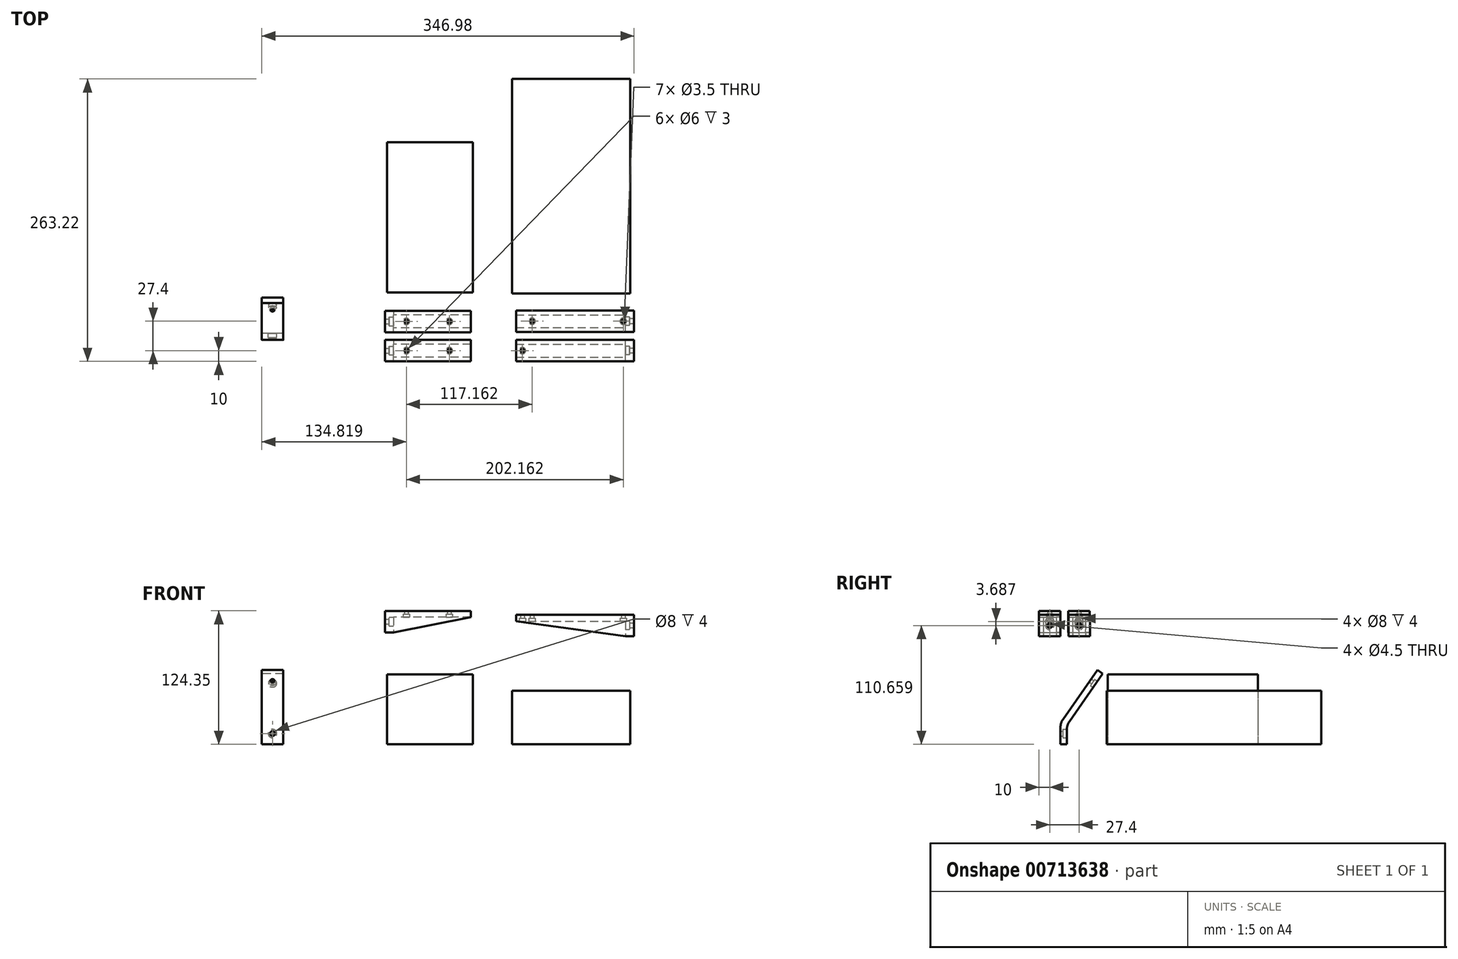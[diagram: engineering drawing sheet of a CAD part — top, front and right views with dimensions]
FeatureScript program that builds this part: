
annotation { "Feature Type Name" : "Feature", "Feature Type Description" : "" }
export const myFeature = defineFeature(function(context is Context, id is Id, definition is map)
    precondition{}
    {
        {
            var Q0;
            Q0=qCreatedBy(makeId("Right.planeOp"),FACE);
            var sketch = newSketch(context, id + "F0", { "sketchPlane" : qUnion([Q0])});
            skLineSegment(sketch, "E0", {"start": v(0, 0) * mm, "end": v(6, 0) * mm});
            skLineSegment(sketch, "E1", {"start": v(6, 0) * mm, "end": v(6, 18.1) * mm});
            skLineSegment(sketch, "E2", {"start": v(6, 18.1) * mm, "end": v(39.33, 65.7) * mm});
            skLineSegment(sketch, "E3", {"start": v(39.33, 65.7) * mm, "end": v(34.41, 69.15) * mm});
            skLineSegment(sketch, "E4", {"start": v(34.41, 69.15) * mm, "end": v(0, 20) * mm});
            skLineSegment(sketch, "E5", {"start": v(0, 20) * mm, "end": v(0, 0) * mm});
            skSolve(sketch);
        }
        {
            var Q0;
            Q0=makeQuery(id+"F0.imprint","IMPRINT",FACE,{"disambiguationData":[TD([[makeQuery(id+"F0.imprint","IMPRINT",EDGE,{"derivedFrom":sQuery(id+"F0.wireOp",EDGE,"E0")}),1.0]])]});
            extrude(context, id + "F1", {"entities" : qUnion([Q0]), "depth" : 20 * mm});
        }
        {
            var Q0;
            Q0=makeQuery(id+"F1.opExtrude","SWEPT_FACE",FACE,{"disambiguationData":[OSD([sQuery(id+"F0.wireOp",EDGE,"E1")])]});
            var sketch = newSketch(context, id + "F2", { "sketchPlane" : qUnion([Q0])});
            skCircle(sketch, "E6", {"center": v(-10, 10) * mm, "radius": 2.25 * mm});
            skPoint(sketch, "E6.centerSnap0", {"position": v(-10, 0) * mm});
            skCircle(sketch, "E7", {"center": v(-10, 10) * mm, "radius": 4 * mm});
            skSolve(sketch);
        }
        {
            var Q0;
            Q0=makeQuery(id+"F1.opExtrude","SWEPT_FACE",FACE,{"disambiguationData":[OSD([sQuery(id+"F0.wireOp",EDGE,"E4")])]});
            var sketch = newSketch(context, id + "F3", { "sketchPlane" : qUnion([Q0])});
            skCircle(sketch, "E8", {"center": v(10, 64.38) * mm, "radius": 1.75 * mm});
            skPoint(sketch, "E8.centerSnap0", {"position": v(10, 16.38) * mm});
            skCircle(sketch, "E9", {"center": v(10, 64.38) * mm, "radius": 3.5 * mm});
            skSolve(sketch);
        }
        {
            var Q0;
            Q0=makeQuery(id+"F3.imprint","IMPRINT",FACE,{"disambiguationData":[TD([[makeQuery(id+"F3.imprint","IMPRINT",EDGE,{"derivedFrom":sQuery(id+"F3.wireOp",EDGE,"E8")}),1.0]])]});
            extrude(context, id + "F4", {"entities" : qUnion([Q0]), "operationType" : NewBodyOperationType.REMOVE, "oppositeDirection" : true, "depth" : 25 * mm});
        }
        {
            var Q0;
            Q0=makeQuery(id+"F1.opExtrude","SWEPT_FACE",FACE,{"disambiguationData":[OSD([sQuery(id+"F0.wireOp",EDGE,"E2")])]});
            var sketch = newSketch(context, id + "F5", { "sketchPlane" : qUnion([Q0])});
            skCircle(sketch, "E10", {"center": v(-10, 64.38) * mm, "radius": 3.5 * mm});
            skSolve(sketch);
        }
        {
            var Q0;
            Q0=makeQuery(id+"F5.imprint","IMPRINT",FACE,{"disambiguationData":[TD([[makeQuery(id+"F5.imprint","IMPRINT",EDGE,{"derivedFrom":sQuery(id+"F5.wireOp",EDGE,"E10")}),1.0]])]});
            extrude(context, id + "F6", {"entities" : qUnion([Q0]), "operationType" : NewBodyOperationType.REMOVE, "oppositeDirection" : true, "depth" : 3 * mm});
        }
        {
            var Q0;
            Q0=makeQuery(id+"F2.imprint","IMPRINT",FACE,{"disambiguationData":[TD([[makeQuery(id+"F2.imprint","IMPRINT",EDGE,{"derivedFrom":sQuery(id+"F2.wireOp",EDGE,"E6")}),1.0]])]});
            extrude(context, id + "F7", {"entities" : qUnion([Q0]), "operationType" : NewBodyOperationType.REMOVE, "oppositeDirection" : true, "depth" : 25 * mm});
        }
        {
            var Q0;
            Q0=makeQuery(id+"F2.imprint","IMPRINT",FACE,{"disambiguationData":[TD([[makeQuery(id+"F2.imprint","IMPRINT",EDGE,{"derivedFrom":sQuery(id+"F2.wireOp",EDGE,"E6")}),-1.0]])]});
            extrude(context, id + "F8", {"entities" : qUnion([Q0]), "operationType" : NewBodyOperationType.REMOVE, "oppositeDirection" : true, "depth" : 4 * mm});
        }
        {
            var Q0;
            Q0=makeQuery(id+"F1.opExtrude","SWEPT_EDGE",EDGE,{"disambiguationData":[OSD([sQuery(id+"F0.wireOp",EDGE,"E1"),sQuery(id+"F0.wireOp",EDGE,"E2")])]});
            var Q1;
            Q1=makeQuery(id+"F1.opExtrude","SWEPT_EDGE",EDGE,{"disambiguationData":[OSD([sQuery(id+"F0.wireOp",EDGE,"E4"),sQuery(id+"F0.wireOp",EDGE,"E5")])]});
            fillet(context, id + "F9", {"entities" : qUnion([Q0, Q1]), "radius" : 13 * mm, "tangentPropagation" : true, "allowEdgeOverflow" : false});
        }
        {
            var Q0;
            Q0=qCreatedBy(makeId("Top.planeOp"),FACE);
            var sketch = newSketch(context, id + "F10", { "sketchPlane" : qUnion([Q0])});
            skLineSegment(sketch, "E11.bottom", {"start": v(116.68, 184.13) * mm, "end": v(196.68, 184.13) * mm});
            skLineSegment(sketch, "E11.top", {"start": v(116.68, 44.13) * mm, "end": v(196.68, 44.13) * mm});
            skLineSegment(sketch, "E11.left", {"start": v(116.68, 184.13) * mm, "end": v(116.68, 44.13) * mm});
            skLineSegment(sketch, "E11.right", {"start": v(196.68, 184.13) * mm, "end": v(196.68, 44.13) * mm});
            skSolve(sketch);
        }
        {
            var Q0;
            Q0=makeQuery(id+"F10.imprint","IMPRINT",FACE,{"disambiguationData":[TD([[makeQuery(id+"F10.imprint","IMPRINT",EDGE,{"derivedFrom":sQuery(id+"F10.wireOp",EDGE,"E11.bottom")}),-1.0]])]});
            extrude(context, id + "F11", {"entities" : qUnion([Q0]), "depth" : 65 * mm});
        }
        {
            var Q0;
            Q0=qCreatedBy(makeId("Top.planeOp"),FACE);
            var sketch = newSketch(context, id + "F12", { "sketchPlane" : qUnion([Q0])});
            skLineSegment(sketch, "E12.bottom", {"start": v(233.36, 43.22) * mm, "end": v(343.36, 43.22) * mm});
            skLineSegment(sketch, "E12.top", {"start": v(233.36, 243.22) * mm, "end": v(343.36, 243.22) * mm});
            skLineSegment(sketch, "E12.left", {"start": v(233.36, 43.22) * mm, "end": v(233.36, 243.22) * mm});
            skLineSegment(sketch, "E12.right", {"start": v(343.36, 43.22) * mm, "end": v(343.36, 243.22) * mm});
            skSolve(sketch);
        }
        {
            var Q0;
            Q0=makeQuery(id+"F12.imprint","IMPRINT",FACE,{"disambiguationData":[TD([[makeQuery(id+"F12.imprint","IMPRINT",EDGE,{"derivedFrom":sQuery(id+"F12.wireOp",EDGE,"E12.bottom")}),1.0]])]});
            extrude(context, id + "F13", {"entities" : qUnion([Q0]), "depth" : 50 * mm});
        }
        {
            var Q0;
            Q0=qCreatedBy(makeId("Front.planeOp"),FACE);
            var sketch = newSketch(context, id + "F14", { "sketchPlane" : qUnion([Q0])});
            skLineSegment(sketch, "E13", {"start": v(114.82, 104.35) * mm, "end": v(122.82, 104.35) * mm});
            skLineSegment(sketch, "E14", {"start": v(114.82, 104.35) * mm, "end": v(114.82, 124.35) * mm});
            skLineSegment(sketch, "E15", {"start": v(114.82, 124.35) * mm, "end": v(194.82, 124.35) * mm});
            skLineSegment(sketch, "E16", {"start": v(194.82, 124.35) * mm, "end": v(194.82, 118.35) * mm});
            skLineSegment(sketch, "E17", {"start": v(194.82, 118.35) * mm, "end": v(122.82, 118.35) * mm});
            skLineSegment(sketch, "E18", {"start": v(122.82, 118.35) * mm, "end": v(122.82, 104.35) * mm});
            skSolve(sketch);
        }
        {
            var Q0;
            Q0=makeQuery(id+"F14.imprint","IMPRINT",FACE,{"disambiguationData":[TD([[makeQuery(id+"F14.imprint","IMPRINT",EDGE,{"derivedFrom":sQuery(id+"F14.wireOp",EDGE,"E13")}),1.0]])]});
            extrude(context, id + "F15", {"entities" : qUnion([Q0]), "depth" : 20 * mm});
        }
        {
            var Q0;
            Q0=makeQuery(id+"F15.opExtrude","SWEPT_FACE",FACE,{"disambiguationData":[OSD([sQuery(id+"F14.wireOp",EDGE,"E18")])]});
            var sketch = newSketch(context, id + "F16", { "sketchPlane" : qUnion([Q0])});
            skCircle(sketch, "E19", {"center": v(-10, 114.35) * mm, "radius": 2.25 * mm});
            skPoint(sketch, "E19.centerSnap0", {"position": v(-10, 104.35) * mm});
            skCircle(sketch, "E20", {"center": v(-10, 114.35) * mm, "radius": 4 * mm});
            skSolve(sketch);
        }
        {
            var Q0;
            Q0=makeQuery(id+"F16.imprint","IMPRINT",FACE,{"disambiguationData":[TD([[makeQuery(id+"F16.imprint","IMPRINT",EDGE,{"derivedFrom":sQuery(id+"F16.wireOp",EDGE,"E19")}),1.0]])]});
            extrude(context, id + "F17", {"entities" : qUnion([Q0]), "operationType" : NewBodyOperationType.REMOVE, "endBound" : BoundingType.THROUGH_ALL, "oppositeDirection" : true, "depth" : 25 * mm});
        }
        {
            var Q0;
            Q0=makeQuery(id+"F16.imprint","IMPRINT",FACE,{"disambiguationData":[TD([[makeQuery(id+"F16.imprint","IMPRINT",EDGE,{"derivedFrom":sQuery(id+"F16.wireOp",EDGE,"E19")}),-1.0]])]});
            extrude(context, id + "F18", {"entities" : qUnion([Q0]), "operationType" : NewBodyOperationType.REMOVE, "oppositeDirection" : true, "depth" : 4 * mm});
        }
        {
            var Q0;
            Q0=makeQuery(id+"F15.opExtrude","CAP_VERTEX",VERTEX,{"disambiguationData":[OSD([sQuery(id+"F14.wireOp",EDGE,"E13"),sQuery(id+"F14.wireOp",EDGE,"E18")])],"isStart":false});
            var Q1;
            Q1=makeQuery(id+"F15.opExtrude","CAP_VERTEX",VERTEX,{"disambiguationData":[OSD([sQuery(id+"F14.wireOp",EDGE,"E13"),sQuery(id+"F14.wireOp",EDGE,"E18")])],"isStart":true});
            var Q2;
            Q2=makeQuery(id+"F15.opExtrude","CAP_VERTEX",VERTEX,{"disambiguationData":[OSD([sQuery(id+"F14.wireOp",EDGE,"E16"),sQuery(id+"F14.wireOp",EDGE,"E17")])],"isStart":false});
            cPlane(context, id + "F19", {"entities" : qUnion([Q0, Q1, Q2]), "cplaneType" : CPlaneType.THREE_POINT, "offset" : 25 * mm, "width" : 150 * mm, "height" : 150 * mm});
        }
        {
            var Q0;
            Q0=qCreatedBy(id+"F19.planeOp",FACE);
            var sketch = newSketch(context, id + "F20", { "sketchPlane" : qUnion([Q0])});
            skLineSegment(sketch, "E21.bottom", {"start": v(140.48, -20) * mm, "end": v(213.83, -20) * mm});
            skLineSegment(sketch, "E21.top", {"start": v(140.48, -16) * mm, "end": v(213.83, -16) * mm});
            skLineSegment(sketch, "E21.left", {"start": v(140.48, -20) * mm, "end": v(140.48, -16) * mm});
            skLineSegment(sketch, "E21.right", {"start": v(213.83, -20) * mm, "end": v(213.83, -16) * mm});
            skLineSegment(sketch, "E22.bottom", {"start": v(140.48, 0) * mm, "end": v(213.83, 0) * mm});
            skLineSegment(sketch, "E22.top", {"start": v(140.48, -4) * mm, "end": v(213.83, -4) * mm});
            skLineSegment(sketch, "E22.left", {"start": v(140.48, 0) * mm, "end": v(140.48, -4) * mm});
            skLineSegment(sketch, "E22.right", {"start": v(213.83, 0) * mm, "end": v(213.83, -4) * mm});
            skSolve(sketch);
        }
        {
            var Q0;
            Q0=qSketchRegion(id+"F20",true);
            extrude(context, id + "F21", {"entities" : qUnion([Q0]), "operationType" : NewBodyOperationType.ADD, "endBound" : BoundingType.UP_TO_NEXT, "depth" : 25 * mm});
        }
        {
            var Q0;
            Q0=makeQuery(id+"F15.opExtrude","SWEPT_FACE",FACE,{"disambiguationData":[OSD([sQuery(id+"F14.wireOp",EDGE,"E17")])]});
            var sketch = newSketch(context, id + "F22", { "sketchPlane" : qUnion([Q0])});
            skCircle(sketch, "E23", {"center": v(174.82, 10) * mm, "radius": 1.75 * mm});
            skPoint(sketch, "E23.centerSnap0", {"position": v(194.82, 10) * mm});
            skCircle(sketch, "E24", {"center": v(174.82, 10) * mm, "radius": 3 * mm});
            skCircle(sketch, "E25", {"center": v(134.82, 10) * mm, "radius": 1.75 * mm});
            skCircle(sketch, "E26", {"center": v(134.82, 10) * mm, "radius": 3 * mm});
            skSolve(sketch);
        }
        {
            var Q0;
            Q0=makeQuery(id+"F22.imprint","IMPRINT",FACE,{"disambiguationData":[TD([[makeQuery(id+"F22.imprint","IMPRINT",EDGE,{"derivedFrom":sQuery(id+"F22.wireOp",EDGE,"E25")}),1.0]])]});
            var Q1;
            Q1=makeQuery(id+"F22.imprint","IMPRINT",FACE,{"disambiguationData":[TD([[makeQuery(id+"F22.imprint","IMPRINT",EDGE,{"derivedFrom":sQuery(id+"F22.wireOp",EDGE,"E23")}),1.0]])]});
            extrude(context, id + "F23", {"entities" : qUnion([Q0, Q1]), "operationType" : NewBodyOperationType.REMOVE, "endBound" : BoundingType.THROUGH_ALL, "oppositeDirection" : true, "depth" : 25 * mm});
        }
        {
            var Q0;
            Q0=makeQuery(id+"F22.imprint","IMPRINT",FACE,{"disambiguationData":[TD([[makeQuery(id+"F22.imprint","IMPRINT",EDGE,{"derivedFrom":sQuery(id+"F22.wireOp",EDGE,"E25")}),-1.0]])]});
            var Q1;
            Q1=makeQuery(id+"F22.imprint","IMPRINT",FACE,{"disambiguationData":[TD([[makeQuery(id+"F22.imprint","IMPRINT",EDGE,{"derivedFrom":sQuery(id+"F22.wireOp",EDGE,"E23")}),-1.0]])]});
            extrude(context, id + "F24", {"entities" : qUnion([Q0, Q1]), "operationType" : NewBodyOperationType.REMOVE, "oppositeDirection" : true, "depth" : 3 * mm});
        }
        {
            var Q0;
            Q0=qCreatedBy(makeId("Front.planeOp"),FACE);
            var sketch = newSketch(context, id + "F25", { "sketchPlane" : qUnion([Q0])});
            skLineSegment(sketch, "E27", {"start": v(338.98, 100.66) * mm, "end": v(346.98, 100.66) * mm});
            skLineSegment(sketch, "E28", {"start": v(346.98, 100.66) * mm, "end": v(346.98, 120.66) * mm});
            skLineSegment(sketch, "E29", {"start": v(346.98, 120.66) * mm, "end": v(236.98, 120.66) * mm});
            skLineSegment(sketch, "E30", {"start": v(236.98, 120.66) * mm, "end": v(236.98, 114.66) * mm});
            skLineSegment(sketch, "E31", {"start": v(236.98, 114.66) * mm, "end": v(338.98, 114.66) * mm});
            skLineSegment(sketch, "E32", {"start": v(338.98, 114.66) * mm, "end": v(338.98, 100.66) * mm});
            skSolve(sketch);
        }
        {
            var Q0;
            Q0=makeQuery(id+"F25.imprint","IMPRINT",FACE,{"disambiguationData":[TD([[makeQuery(id+"F25.imprint","IMPRINT",EDGE,{"derivedFrom":sQuery(id+"F25.wireOp",EDGE,"E27")}),1.0]])]});
            extrude(context, id + "F26", {"entities" : qUnion([Q0]), "depth" : 20 * mm});
        }
        {
            var Q0;
            Q0=makeQuery(id+"F26.opExtrude","SWEPT_FACE",FACE,{"disambiguationData":[OSD([sQuery(id+"F25.wireOp",EDGE,"E32")])]});
            var sketch = newSketch(context, id + "F27", { "sketchPlane" : qUnion([Q0])});
            skCircle(sketch, "E33", {"center": v(10, 110.66) * mm, "radius": 2.25 * mm});
            skPoint(sketch, "E33.centerSnap0", {"position": v(10, 100.66) * mm});
            skCircle(sketch, "E34", {"center": v(10, 110.66) * mm, "radius": 4 * mm});
            skSolve(sketch);
        }
        {
            var Q0;
            Q0=makeQuery(id+"F27.imprint","IMPRINT",FACE,{"disambiguationData":[TD([[makeQuery(id+"F27.imprint","IMPRINT",EDGE,{"derivedFrom":sQuery(id+"F27.wireOp",EDGE,"E33")}),-1.0]])]});
            extrude(context, id + "F28", {"entities" : qUnion([Q0]), "operationType" : NewBodyOperationType.REMOVE, "oppositeDirection" : true, "depth" : 4 * mm});
        }
        {
            var Q0;
            Q0=makeQuery(id+"F28.boolean.opBoolean","SPLIT",FACE,{"disambiguationData":[TD([makeQuery(id+"F28.opExtrude","SWEPT_FACE",FACE,{"disambiguationData":[OSD([sQuery(id+"F27.wireOp",EDGE,"E33")])]})])],"derivedFrom":makeQuery(id+"F26.opExtrude","SWEPT_FACE",FACE,{"disambiguationData":[OSD([sQuery(id+"F25.wireOp",EDGE,"E32")])]})});
            extrude(context, id + "F29", {"entities" : qUnion([Q0]), "operationType" : NewBodyOperationType.REMOVE, "endBound" : BoundingType.THROUGH_ALL, "oppositeDirection" : true, "depth" : 25 * mm});
        }
        {
            var Q0;
            Q0=makeQuery(id+"F26.opExtrude","CAP_VERTEX",VERTEX,{"disambiguationData":[OSD([sQuery(id+"F25.wireOp",EDGE,"E30"),sQuery(id+"F25.wireOp",EDGE,"E31")])],"isStart":false});
            var Q1;
            Q1=makeQuery(id+"F26.opExtrude","CAP_VERTEX",VERTEX,{"disambiguationData":[OSD([sQuery(id+"F25.wireOp",EDGE,"E30"),sQuery(id+"F25.wireOp",EDGE,"E31")])],"isStart":true});
            var Q2;
            Q2=makeQuery(id+"F26.opExtrude","CAP_VERTEX",VERTEX,{"disambiguationData":[OSD([sQuery(id+"F25.wireOp",EDGE,"E27"),sQuery(id+"F25.wireOp",EDGE,"E32")])],"isStart":false});
            cPlane(context, id + "F30", {"entities" : qUnion([Q0, Q1, Q2]), "cplaneType" : CPlaneType.THREE_POINT, "offset" : 25 * mm, "width" : 150 * mm, "height" : 150 * mm});
        }
        {
            var Q0;
            Q0=qCreatedBy(id+"F30.planeOp",FACE);
            var sketch = newSketch(context, id + "F31", { "sketchPlane" : qUnion([Q0])});
            skLineSegment(sketch, "E35.bottom", {"start": v(219.19, -20) * mm, "end": v(322.14, -20) * mm});
            skLineSegment(sketch, "E35.top", {"start": v(219.19, -16) * mm, "end": v(322.14, -16) * mm});
            skLineSegment(sketch, "E35.left", {"start": v(219.19, -20) * mm, "end": v(219.19, -16) * mm});
            skLineSegment(sketch, "E35.right", {"start": v(322.14, -20) * mm, "end": v(322.14, -16) * mm});
            skLineSegment(sketch, "E36.bottom", {"start": v(219.19, -4) * mm, "end": v(322.14, -4) * mm});
            skLineSegment(sketch, "E36.top", {"start": v(219.19, 0) * mm, "end": v(322.14, 0) * mm});
            skLineSegment(sketch, "E36.left", {"start": v(219.19, -4) * mm, "end": v(219.19, 0) * mm});
            skLineSegment(sketch, "E36.right", {"start": v(322.14, -4) * mm, "end": v(322.14, 0) * mm});
            skSolve(sketch);
        }
        {
            var Q0;
            Q0=makeQuery(id+"F31.imprint","IMPRINT",FACE,{"disambiguationData":[TD([[makeQuery(id+"F31.imprint","IMPRINT",EDGE,{"derivedFrom":sQuery(id+"F31.wireOp",EDGE,"E35.bottom")}),1.0]])]});
            var Q1;
            Q1=makeQuery(id+"F31.imprint","IMPRINT",FACE,{"disambiguationData":[TD([[makeQuery(id+"F31.imprint","IMPRINT",EDGE,{"derivedFrom":sQuery(id+"F31.wireOp",EDGE,"E36.bottom")}),1.0]])]});
            extrude(context, id + "F32", {"entities" : qUnion([Q0, Q1]), "operationType" : NewBodyOperationType.ADD, "endBound" : BoundingType.UP_TO_NEXT, "depth" : 25 * mm});
        }
        {
            var Q0;
            Q0=makeQuery(id+"F26.opExtrude","SWEPT_BODY",BODY,{"disambiguationData":[OSD([sQuery(id+"F25.wireOp",EDGE,"E27"),sQuery(id+"F25.wireOp",EDGE,"E28"),sQuery(id+"F25.wireOp",EDGE,"E29"),sQuery(id+"F25.wireOp",EDGE,"E30"),sQuery(id+"F25.wireOp",EDGE,"E31"),sQuery(id+"F25.wireOp",EDGE,"E32")])]});
            transform(context, id + "F33", {"entities" : qUnion([Q0]), "transformType" : TransformType.TRANSLATION_3D, "dx" : 0 * mm, "dy" : 27.4 * mm, "dz" : 0 * mm, "makeCopy" : true});
        }
        {
            var Q0;
            Q0=makeQuery(id+"F26.opExtrude","SWEPT_FACE",FACE,{"disambiguationData":[OSD([sQuery(id+"F25.wireOp",EDGE,"E31")])]});
            var sketch = newSketch(context, id + "F34", { "sketchPlane" : qUnion([Q0])});
            skCircle(sketch, "E37", {"center": v(242.98, 10) * mm, "radius": 1.75 * mm});
            skPoint(sketch, "E37.centerSnap0", {"position": v(236.98, 10) * mm});
            skCircle(sketch, "E38", {"center": v(242.98, 10) * mm, "radius": 3 * mm});
            skSolve(sketch);
        }
        {
            var Q0;
            Q0=makeQuery(id+"F33.opPattern","COPY",FACE,{"derivedFrom":makeQuery(id+"F26.opExtrude","SWEPT_FACE",FACE,{"disambiguationData":[OSD([sQuery(id+"F25.wireOp",EDGE,"E31")])]}),"instanceName":"1"});
            var sketch = newSketch(context, id + "F35", { "sketchPlane" : qUnion([Q0])});
            skCircle(sketch, "E39", {"center": v(251.98, -17.4) * mm, "radius": 1.75 * mm});
            skPoint(sketch, "E39.centerSnap0", {"position": v(236.98, -17.4) * mm});
            skCircle(sketch, "E40", {"center": v(251.98, -17.4) * mm, "radius": 3 * mm});
            skCircle(sketch, "E41", {"center": v(336.98, -17.4) * mm, "radius": 1.75 * mm});
            skCircle(sketch, "E42", {"center": v(336.98, -17.4) * mm, "radius": 3 * mm});
            skSolve(sketch);
        }
        {
            var Q0;
            Q0=makeQuery(id+"F34.imprint","IMPRINT",FACE,{"disambiguationData":[TD([[makeQuery(id+"F34.imprint","IMPRINT",EDGE,{"derivedFrom":sQuery(id+"F34.wireOp",EDGE,"E37")}),-1.0]])]});
            var Q1;
            Q1=makeQuery(id+"F35.imprint","IMPRINT",FACE,{"disambiguationData":[TD([[makeQuery(id+"F35.imprint","IMPRINT",EDGE,{"derivedFrom":sQuery(id+"F35.wireOp",EDGE,"E39")}),-1.0]])]});
            var Q2;
            Q2=makeQuery(id+"F35.imprint","IMPRINT",FACE,{"disambiguationData":[TD([[makeQuery(id+"F35.imprint","IMPRINT",EDGE,{"derivedFrom":sQuery(id+"F35.wireOp",EDGE,"E41")}),-1.0]])]});
            extrude(context, id + "F36", {"entities" : qUnion([Q0, Q1, Q2]), "operationType" : NewBodyOperationType.REMOVE, "oppositeDirection" : true, "depth" : 3 * mm});
        }
        {
            var Q0;
            Q0=makeQuery(id+"F36.boolean.opBoolean","SPLIT",FACE,{"disambiguationData":[TD([makeQuery(id+"F36.opExtrude","SWEPT_FACE",FACE,{"disambiguationData":[OSD([sQuery(id+"F34.wireOp",EDGE,"E37")])]})])],"derivedFrom":makeQuery(id+"F26.opExtrude","SWEPT_FACE",FACE,{"disambiguationData":[OSD([sQuery(id+"F25.wireOp",EDGE,"E31")])]})});
            var Q1;
            Q1=makeQuery(id+"F36.boolean.opBoolean","SPLIT",FACE,{"disambiguationData":[TD([makeQuery(id+"F36.opExtrude","SWEPT_FACE",FACE,{"disambiguationData":[OSD([sQuery(id+"F35.wireOp",EDGE,"E39")])]})])],"derivedFrom":makeQuery(id+"F33.opPattern","COPY",FACE,{"derivedFrom":makeQuery(id+"F26.opExtrude","SWEPT_FACE",FACE,{"disambiguationData":[OSD([sQuery(id+"F25.wireOp",EDGE,"E31")])]}),"instanceName":"1"})});
            var Q2;
            Q2=makeQuery(id+"F36.boolean.opBoolean","SPLIT",FACE,{"disambiguationData":[TD([makeQuery(id+"F36.opExtrude","SWEPT_FACE",FACE,{"disambiguationData":[OSD([sQuery(id+"F35.wireOp",EDGE,"E41")])]})])],"derivedFrom":makeQuery(id+"F33.opPattern","COPY",FACE,{"derivedFrom":makeQuery(id+"F26.opExtrude","SWEPT_FACE",FACE,{"disambiguationData":[OSD([sQuery(id+"F25.wireOp",EDGE,"E31")])]}),"instanceName":"1"})});
            extrude(context, id + "F37", {"entities" : qUnion([Q0, Q1, Q2]), "operationType" : NewBodyOperationType.REMOVE, "endBound" : BoundingType.THROUGH_ALL, "oppositeDirection" : true, "depth" : 25 * mm});
        }
        {
            var Q0;
            {var subQ0=sQuery(id+"F35.wireOp",EDGE,"E42");var subQ1=sQuery(id+"F25.wireOp",EDGE,"E32");var subQ2=sQuery(id+"F25.wireOp",EDGE,"E31");var subQ3=sQuery(id+"F25.wireOp",EDGE,"E30");var subQ4=sQuery(id+"F25.wireOp",EDGE,"E29");var subQ5=sQuery(id+"F25.wireOp",EDGE,"E28");var subQ6=sQuery(id+"F25.wireOp",EDGE,"E27");var subQ10=makeQuery(id+"F26.opExtrude","SWEPT_EDGE",EDGE,{"disambiguationData":[OSD([subQ2,subQ1])]});var subQ11=makeQuery(id+"F33.opPattern","COPY",EDGE,{"derivedFrom":makeQuery(id+"F28.boolean.opBoolean","SPLIT",EDGE,{"disambiguationData":[TD([makeQuery(id+"F26.opExtrude","CAP_FACE",FACE,{"disambiguationData":[OSD([subQ6,subQ5,subQ4,subQ3,subQ2,subQ1])],"isStart":true})])],"derivedFrom":subQ10}),"instanceName":"1"});var subQ12=makeQuery(id+"F35.imprint","INTERSECT",VERTEX,{"derivedFrom":[subQ11,subQ0]});Q0=makeQuery(id+"F35.imprint","IMPRINT",FACE,{"disambiguationData":[TD([[makeQuery(id+"F35.imprint","IMPRINT",EDGE,{"disambiguationData":[TD([[subQ12,-1.0]])],"derivedFrom":subQ0}),1.0]])]});}
            extrude(context, id + "F38", {"entities" : qUnion([Q0]), "operationType" : NewBodyOperationType.REMOVE, "endBound" : BoundingType.SYMMETRIC, "oppositeDirection" : true, "depth" : 6 * mm});
        }
        {
            var Q0;
            Q0=makeQuery(id+"F15.opExtrude","SWEPT_BODY",BODY,{"disambiguationData":[OSD([sQuery(id+"F14.wireOp",EDGE,"E13"),sQuery(id+"F14.wireOp",EDGE,"E14"),sQuery(id+"F14.wireOp",EDGE,"E15"),sQuery(id+"F14.wireOp",EDGE,"E16"),sQuery(id+"F14.wireOp",EDGE,"E17"),sQuery(id+"F14.wireOp",EDGE,"E18")])]});
            transform(context, id + "F39", {"entities" : qUnion([Q0]), "transformType" : TransformType.TRANSLATION_3D, "dx" : 0 * mm, "dy" : 27.2 * mm, "dz" : 0 * mm, "makeCopy" : true});
        }
    });
